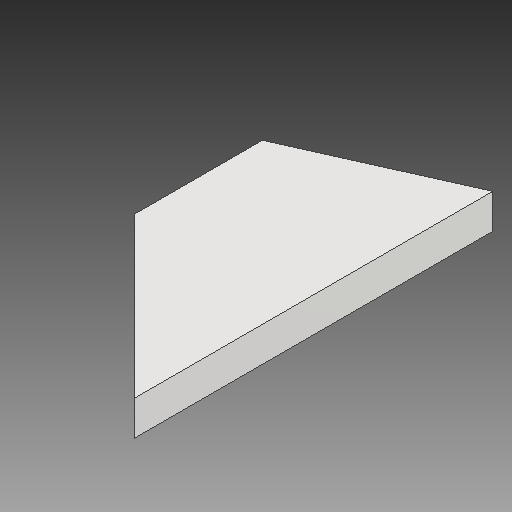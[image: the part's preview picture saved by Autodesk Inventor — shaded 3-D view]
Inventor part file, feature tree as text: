
AUTODESK INVENTOR PART (.ipt)
format: ipt  version: 2018 (Build 220112000, 112)  size: 78,336 bytes
history: native  units: in
note: dims shown in document units (in); Inventor stores cm internally (conversion verified against a paired STEP export)
features: chamfer x1
ambient origin geometry x8: Origin, YZ Plane, XZ Plane, XY Plane, X Axis, Y Axis, Z Axis, Center Point
bodies: Solid1 (feature_tree)
feature tree (1):
  chamfer  "Chamfer1"  [1 undecoded]
note: 1 required parameter value undecoded (feature->parameter linkage not recoverable at this tier; creation-order binding heuristic only, values carry confidence <= 0.55)
